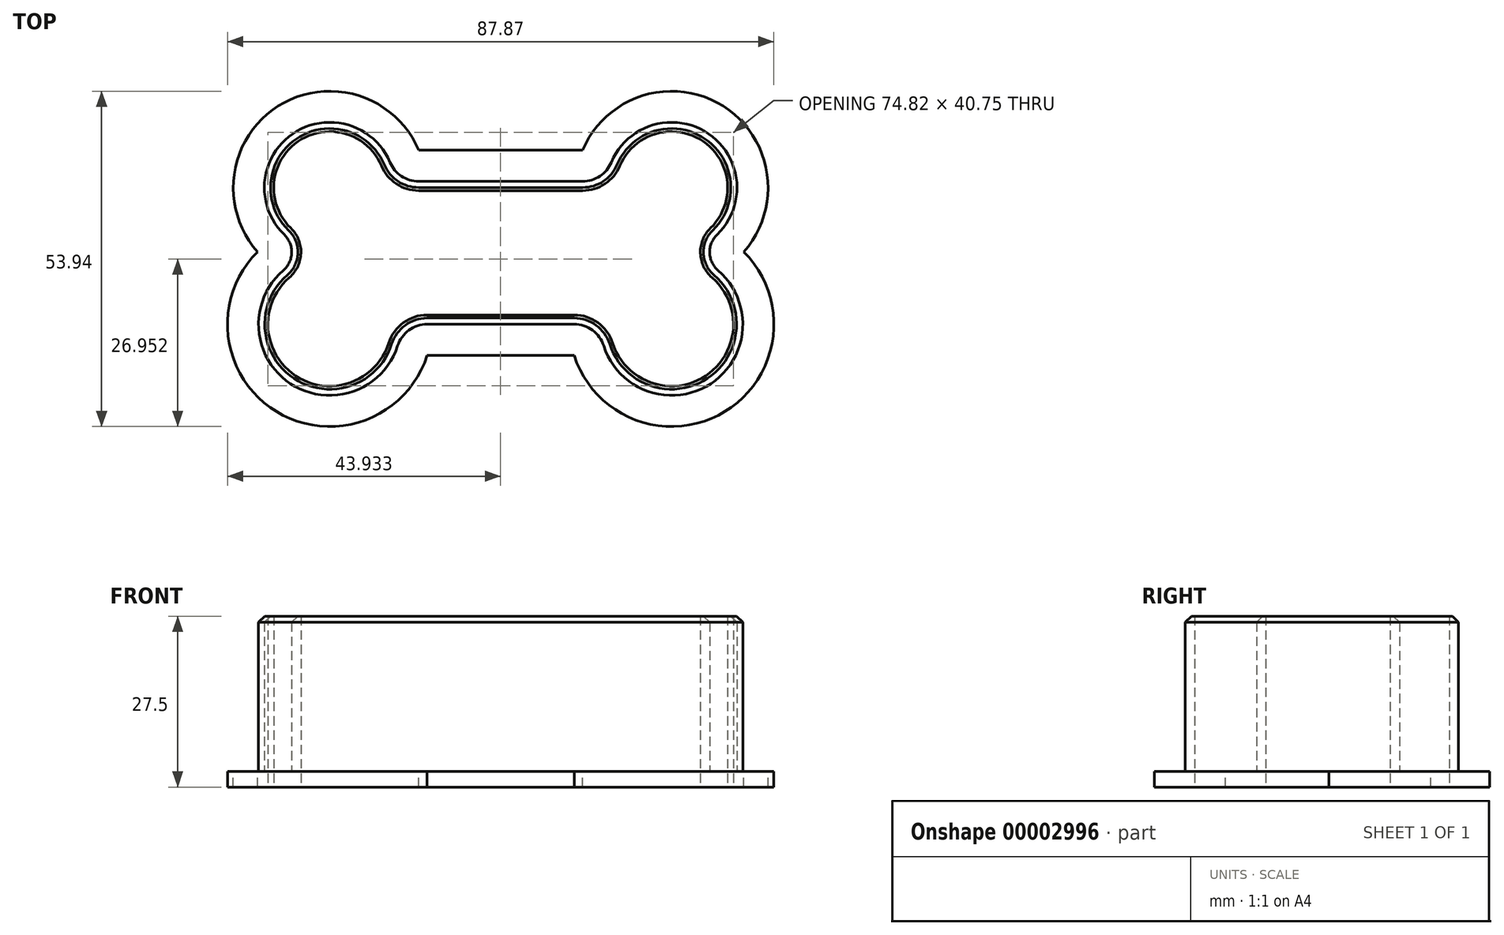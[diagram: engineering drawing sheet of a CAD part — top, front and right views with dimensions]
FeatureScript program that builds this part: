
annotation { "Feature Type Name" : "Feature", "Feature Type Description" : "" }
export const myFeature = defineFeature(function(context is Context, id is Id, definition is map)
    precondition{}
    {
        {
            var Q0;
            Q0=qCreatedBy(makeId("Top.planeOp"),FACE);
            var sketch = newSketch(context, id + "F0", { "sketchPlane" : qUnion([Q0])});
            skLineSegment(sketch, "E0.bottom", {"start": v(-11.31, 11.39) * mm, "end": v(15.06, 11.39) * mm});
            skLineSegment(sketch, "E0.top", {"start": v(-9.94, -11.61) * mm, "end": v(13.7, -11.61) * mm});
            skArc(sketch, "E1", {"start": v(-15.92, 14.45) * mm, "mid": v(-31.56, 19.04) * mm, "end": v(-32.93, 2.8) * mm});
            skArc(sketch, "E2", {"start": v(-33.09, -2.94) * mm, "mid": v(-31.92, -21.16) * mm, "end": v(-14.7, -15.1) * mm});
            skLineSegment(sketch, "E3", {"start": v(1.87, 11.39) * mm, "end": v(1.87, -11.61) * mm, "construction": true});
            skArc(sketch, "E4.0.MirrorC", {"start": v(19.66, 14.45) * mm, "mid": v(35.3, 19.04) * mm, "end": v(36.67, 2.8) * mm});
            skArc(sketch, "E4.1.MirrorC", {"start": v(36.84, -2.94) * mm, "mid": v(35.67, -21.16) * mm, "end": v(18.45, -15.1) * mm});
            skArc(sketch, "E5", {"start": v(-33.09, -2.94) * mm, "mid": v(-31.74, -0.11) * mm, "end": v(-32.93, 2.8) * mm});
            skArc(sketch, "E6.0.MirrorCS", {"start": v(36.84, -2.94) * mm, "mid": v(35.49, -0.11) * mm, "end": v(36.67, 2.8) * mm});
            skLineSegment(sketch, "E6.2.MirrorCS", {"start": v(13.7, -11.61) * mm, "end": v(-9.94, -11.61) * mm});
            skLineSegment(sketch, "E6.4.MirrorCS", {"start": v(15.06, 11.39) * mm, "end": v(-11.31, 11.39) * mm});
            skPoint(sketch, "E7.visualSharp", {"position": v(-15.14, 11.39) * mm});
            skArc(sketch, "E7.filletArc", {"start": v(-15.92, 14.45) * mm, "mid": v(-14.08, 12.22) * mm, "end": v(-11.31, 11.39) * mm});
            skPoint(sketch, "E8.visualSharp", {"position": v(-14.17, -11.61) * mm});
            skArc(sketch, "E8.filletArc", {"start": v(-9.94, -11.61) * mm, "mid": v(-12.9, -12.57) * mm, "end": v(-14.7, -15.1) * mm});
            skPoint(sketch, "E9.visualSharp", {"position": v(17.91, -11.61) * mm});
            skArc(sketch, "E9.filletArc", {"start": v(18.45, -15.1) * mm, "mid": v(16.64, -12.57) * mm, "end": v(13.7, -11.61) * mm});
            skPoint(sketch, "E10.visualSharp", {"position": v(18.89, 11.39) * mm});
            skArc(sketch, "E10.filletArc", {"start": v(15.06, 11.39) * mm, "mid": v(17.82, 12.22) * mm, "end": v(19.66, 14.45) * mm});
            skLineSegment(sketch, "E11", {"start": v(-31.74, -0.11) * mm, "end": v(35.49, -0.11) * mm, "construction": true});
            skArc(sketch, "E12.0", {"start": v(-11.31, 16.39) * mm, "mid": v(-33.9, 23.48) * mm, "end": v(-37.21, 0.05) * mm});
            skLineSegment(sketch, "E12.1", {"start": v(-11.31, 16.39) * mm, "end": v(15.06, 16.39) * mm});
            skArc(sketch, "E12.2", {"start": v(15.06, 16.39) * mm, "mid": v(37.64, 23.48) * mm, "end": v(40.96, 0.05) * mm});
            skArc(sketch, "E12.3", {"start": v(40.96, 0.05) * mm, "mid": v(37.93, -25.65) * mm, "end": v(13.7, -16.61) * mm});
            skLineSegment(sketch, "E12.4", {"start": v(-9.94, -16.61) * mm, "end": v(13.7, -16.61) * mm});
            skArc(sketch, "E12.5", {"start": v(-37.21, 0.05) * mm, "mid": v(-34.19, -25.65) * mm, "end": v(-9.94, -16.61) * mm});
            skArc(sketch, "E13.0", {"start": v(-17.3, 13.86) * mm, "mid": v(-14.9, 10.97) * mm, "end": v(-11.31, 9.89) * mm});
            skLineSegment(sketch, "E13.1", {"start": v(-11.31, 9.89) * mm, "end": v(15.06, 9.89) * mm});
            skArc(sketch, "E13.2", {"start": v(15.06, 9.89) * mm, "mid": v(18.65, 10.97) * mm, "end": v(21.05, 13.86) * mm});
            skArc(sketch, "E13.3", {"start": v(21.05, 13.86) * mm, "mid": v(34.46, 17.8) * mm, "end": v(35.63, 3.87) * mm});
            skArc(sketch, "E13.4", {"start": v(35.86, -4.08) * mm, "mid": v(33.99, -0.15) * mm, "end": v(35.63, 3.87) * mm});
            skArc(sketch, "E13.5", {"start": v(-17.3, 13.86) * mm, "mid": v(-30.71, 17.8) * mm, "end": v(-31.88, 3.87) * mm});
            skArc(sketch, "E13.6", {"start": v(35.86, -4.08) * mm, "mid": v(34.84, -19.9) * mm, "end": v(19.88, -14.63) * mm});
            skArc(sketch, "E13.7", {"start": v(19.88, -14.63) * mm, "mid": v(17.52, -11.36) * mm, "end": v(13.7, -10.11) * mm});
            skLineSegment(sketch, "E13.8", {"start": v(-9.94, -10.11) * mm, "end": v(13.7, -10.11) * mm});
            skArc(sketch, "E13.9", {"start": v(-9.94, -10.11) * mm, "mid": v(-13.78, -11.36) * mm, "end": v(-16.14, -14.63) * mm});
            skArc(sketch, "E13.10", {"start": v(-32.1, -4.08) * mm, "mid": v(-31.1, -19.9) * mm, "end": v(-16.14, -14.63) * mm});
            skArc(sketch, "E13.11", {"start": v(-32.1, -4.08) * mm, "mid": v(-30.24, -0.15) * mm, "end": v(-31.88, 3.87) * mm});
            skSolve(sketch);
        }
        {
            var Q0;
            Q0=makeQuery(id+"F0.imprint","IMPRINT",FACE,{"disambiguationData":[TD([[makeQuery(id+"F0.imprint","IMPRINT",EDGE,{"derivedFrom":sQuery(id+"F0.wireOp",EDGE,"E1")}),1.0]])]});
            extrude(context, id + "F1", {"entities" : qUnion([Q0]), "depth" : 25 * mm});
        }
        {
            var Q0;
            Q0=makeQuery(id+"F0.imprint","IMPRINT",FACE,{"disambiguationData":[TD([[makeQuery(id+"F0.imprint","IMPRINT",EDGE,{"derivedFrom":sQuery(id+"F0.wireOp",EDGE,"E1")}),-1.0]])]});
            var Q1;
            Q1=makeQuery(id+"F0.imprint","IMPRINT",FACE,{"disambiguationData":[TD([[makeQuery(id+"F0.imprint","IMPRINT",EDGE,{"derivedFrom":sQuery(id+"F0.wireOp",EDGE,"E1")}),1.0]])]});
            extrude(context, id + "F2", {"entities" : qUnion([Q0, Q1]), "operationType" : NewBodyOperationType.ADD, "oppositeDirection" : true, "depth" : 2.5 * mm});
        }
        {
            var Q0;
            Q0=makeQuery(id+"F1.opExtrude","CAP_EDGE",EDGE,{"disambiguationData":[OSD([sQuery(id+"F0.wireOp",EDGE,"E6.2.MirrorCS")])],"isStart":false});
            var Q1;
            Q1=makeQuery(id+"F1.opExtrude","CAP_EDGE",EDGE,{"disambiguationData":[OSD([sQuery(id+"F0.wireOp",EDGE,"E8.filletArc")])],"isStart":false});
            var Q2;
            Q2=makeQuery(id+"F1.opExtrude","CAP_EDGE",EDGE,{"disambiguationData":[OSD([sQuery(id+"F0.wireOp",EDGE,"E2")])],"isStart":false});
            var Q3;
            Q3=makeQuery(id+"F1.opExtrude","CAP_EDGE",EDGE,{"disambiguationData":[OSD([sQuery(id+"F0.wireOp",EDGE,"E5")])],"isStart":false});
            var Q4;
            Q4=makeQuery(id+"F1.opExtrude","CAP_EDGE",EDGE,{"disambiguationData":[OSD([sQuery(id+"F0.wireOp",EDGE,"E1")])],"isStart":false});
            var Q5;
            Q5=makeQuery(id+"F1.opExtrude","CAP_EDGE",EDGE,{"disambiguationData":[OSD([sQuery(id+"F0.wireOp",EDGE,"E7.filletArc")])],"isStart":false});
            var Q6;
            Q6=makeQuery(id+"F1.opExtrude","CAP_EDGE",EDGE,{"disambiguationData":[OSD([sQuery(id+"F0.wireOp",EDGE,"E6.4.MirrorCS")])],"isStart":false});
            var Q7;
            Q7=makeQuery(id+"F1.opExtrude","CAP_EDGE",EDGE,{"disambiguationData":[OSD([sQuery(id+"F0.wireOp",EDGE,"E10.filletArc")])],"isStart":false});
            var Q8;
            Q8=makeQuery(id+"F1.opExtrude","CAP_EDGE",EDGE,{"disambiguationData":[OSD([sQuery(id+"F0.wireOp",EDGE,"E4.0.MirrorC")])],"isStart":false});
            var Q9;
            Q9=makeQuery(id+"F1.opExtrude","CAP_EDGE",EDGE,{"disambiguationData":[OSD([sQuery(id+"F0.wireOp",EDGE,"E6.0.MirrorCS")])],"isStart":false});
            var Q10;
            Q10=makeQuery(id+"F1.opExtrude","CAP_EDGE",EDGE,{"disambiguationData":[OSD([sQuery(id+"F0.wireOp",EDGE,"E4.1.MirrorC")])],"isStart":false});
            var Q11;
            Q11=makeQuery(id+"F1.opExtrude","CAP_EDGE",EDGE,{"disambiguationData":[OSD([sQuery(id+"F0.wireOp",EDGE,"E9.filletArc")])],"isStart":false});
            chamfer(context, id + "F3", {"entities" : qUnion([Q0, Q1, Q2, Q3, Q4, Q5, Q6, Q7, Q8, Q9, Q10, Q11]), "width" : 1 * mm, "tangentPropagation" : true});
        }
    });
